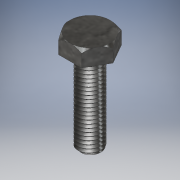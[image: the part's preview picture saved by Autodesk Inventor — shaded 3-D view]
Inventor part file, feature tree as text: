
AUTODESK INVENTOR PART (.ipt)
format: ipt  version: 2019 (Build 230136000, 136)  size: 593,408 bytes
history: native  units: mm
features: sketch x4, extrude x3, fillet x2, helix x1
ambient origin geometry x8: Origin, YZ Plane, XZ Plane, XY Plane, X Axis, Y Axis, Z Axis, Center Point
bodies: Solid1 (feature_tree)
feature tree (10):
  extrude  "Extrusion1"  Depth=7.5mm TaperAngle=0.0deg
  extrude  "Extrusion2"  Depth=11.0mm
  extrude  "Extrusion3"  Depth=1.7mm
  fillet  "Fillet1"  Radius=1.0mm
  fillet  "Fillet2"  Radius=1.7mm
  helix  "Coil1"  [1 undecoded]
  sketch  "Sketch1"  dims[d0=19.0mm d1=7.5mm d2=0.0mm]
  sketch  "Sketch2"  dims[d3=7.5mm d4=45.0deg d5=11.0mm]
  sketch  "Sketch3"  dims[d6=40.0mm d7=0.0mm d8=1.0mm d9=1.0mm d10=1.7mm d11=60.0deg]
  sketch  "Sketch4"  dims[d12=2.0mm d13=0.2mm d14=1.7mm d15=40.0mm d16=10.0mm d17=0.0mm d18=90.0deg d19=90.0deg d20=0.0mm d21=0.0mm]
note: 1 required parameter value undecoded (feature->parameter linkage not recoverable at this tier; creation-order binding heuristic only, values carry confidence <= 0.55)
